# Revit family: QF_ELECTROLUXPROFESSIONAL_602180_EVP16D
name_source: partatom
category: Specialty Equipment
revit_build: Autodesk Revit 2018 (Build: 20190510_1515(x64)
units: mm (PartAtom-declared; Revit-internal decimal feet)

## family parameters
Always vertical = Yes
Cut with Voids When Loaded = No
Part Type = Normal
Room Calculation Point = No
Round Connector Dimension = Use Diameter
Shared = No
Work Plane-Based = No

## types (1)
- Standard
    Accessory = Yes
    Cold Water Size = 0 mm
    Compressed Air Pressure = 0.0 Pa
    Compressed Air Size = 0 mm
    Compressed Air Volume = 0.0 L/s
    Condensate Return Size = 0 mm
    Cycle = 60 Hz
    Depth = 594 mm  [stored 1.94882 ft]
    Depth Actual = 594 mm  [stored 1.94882 ft]
    Description = VACUUM PACKER 16 M3/H, TABLE TOP, DIGITAL DISPLAY
    Direct Waste Size = 0 mm
    FeetFront = 457 mm  [stored 1.49934 ft]
    FeetLeft = 474 mm  [stored 1.55512 ft]
    Gas Input Pressure = 0
    Gas KW = 0
    Gas Size = 0 mm
    HP = 1.1 HP
    Height = 440 mm  [stored 1.44357 ft]
    Height Actual = 440 mm  [stored 1.44357 ft]
    Hot Water Size = 0 mm
    Item Number = 602180
    Length Actual = 531 mm  [stored 1.74213 ft]
    Manufacturer = Electrolux Professional
    Max_Height = 830 mm  [stored 2.7231 ft]
    Model = EVP16D
    Phase = 0
    Refrigerant Compressor Remote = Yes
    Refrigeration Liquid Line Size = 0 mm
    Refrigeration Suction Line Size = 0 mm
    Steam Pounds per Hour = 0
    Steam Supply Maximum Pressure = 0.0 Pa
    Steam Supply Minimum Pressure = 0.0 Pa
    Steam Supply Size = 0 mm
    URL = http://professional.electrolux.com
    URL Manufacturer = http://professional.electrolux.com
    Volts = 220 V
    Watts = 0 W
    Weight = 61.00 kg
    Width = 531 mm  [stored 1.74213 ft]

note: source unit labels omitted for Gas Input Pressure — the stored unit's dimension contradicts the parameter name (converter mislabeling)

note: [stored X ft] marks values corroborated as IEEE doubles in the binary element streams (Revit-internal decimal feet)

## geometry (parser evidence)
native form markers: Sweep x8
no freeform markers — native parametric forms only
